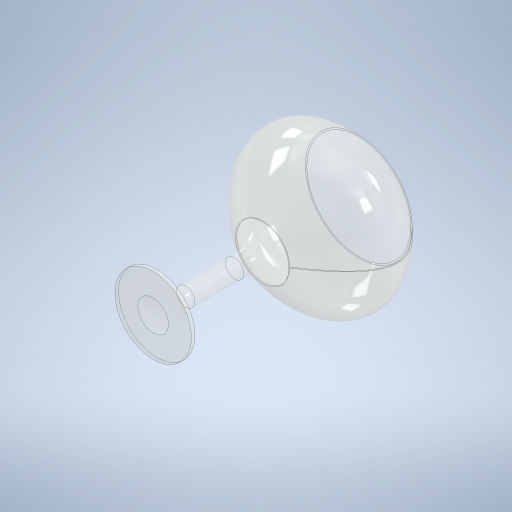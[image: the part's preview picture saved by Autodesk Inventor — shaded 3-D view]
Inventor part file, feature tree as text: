
AUTODESK INVENTOR PART (.ipt)
format: ipt  version: 2024 (Build 280153000, 153)  size: 424,960 bytes
history: native  units: mm
features: revolve x2, sketch x2, projected_geometry x2, shell x1, plane x1
ambient origin geometry x8: Origin, YZ Plane, XZ Plane, XY Plane, X Axis, Y Axis, Z Axis, Center Point
bodies: Volumenkörper1 (feature_tree)
feature tree (8):
  revolve  "Umdrehung1"
  shell  "Wandung1"  Thickness=95.0mm
  plane  "Arbeitsebene1"
  revolve  "Umdrehung2"
  sketch  "Skizze1"  dims[d10=90.0deg]
  sketch  "Skizze3"  dims[d12=105.0mm d13=200.0mm d14=140.0mm d15=120.0mm d16=16.815037mm d17=40.59576mm d18=72.568883mm d20=52.629802mm d21=1.0mm d22=0.0mm d24=200.0mm d25=30.0mm d26=80.0mm d27=75.0mm d28=4.0mm d30=9.0mm d32=29.921817mm d33=3.5mm d34=90.0deg]
  projected_geometry  "Projizierte Kontur1"
  projected_geometry  "Projizierte Kontur2"
